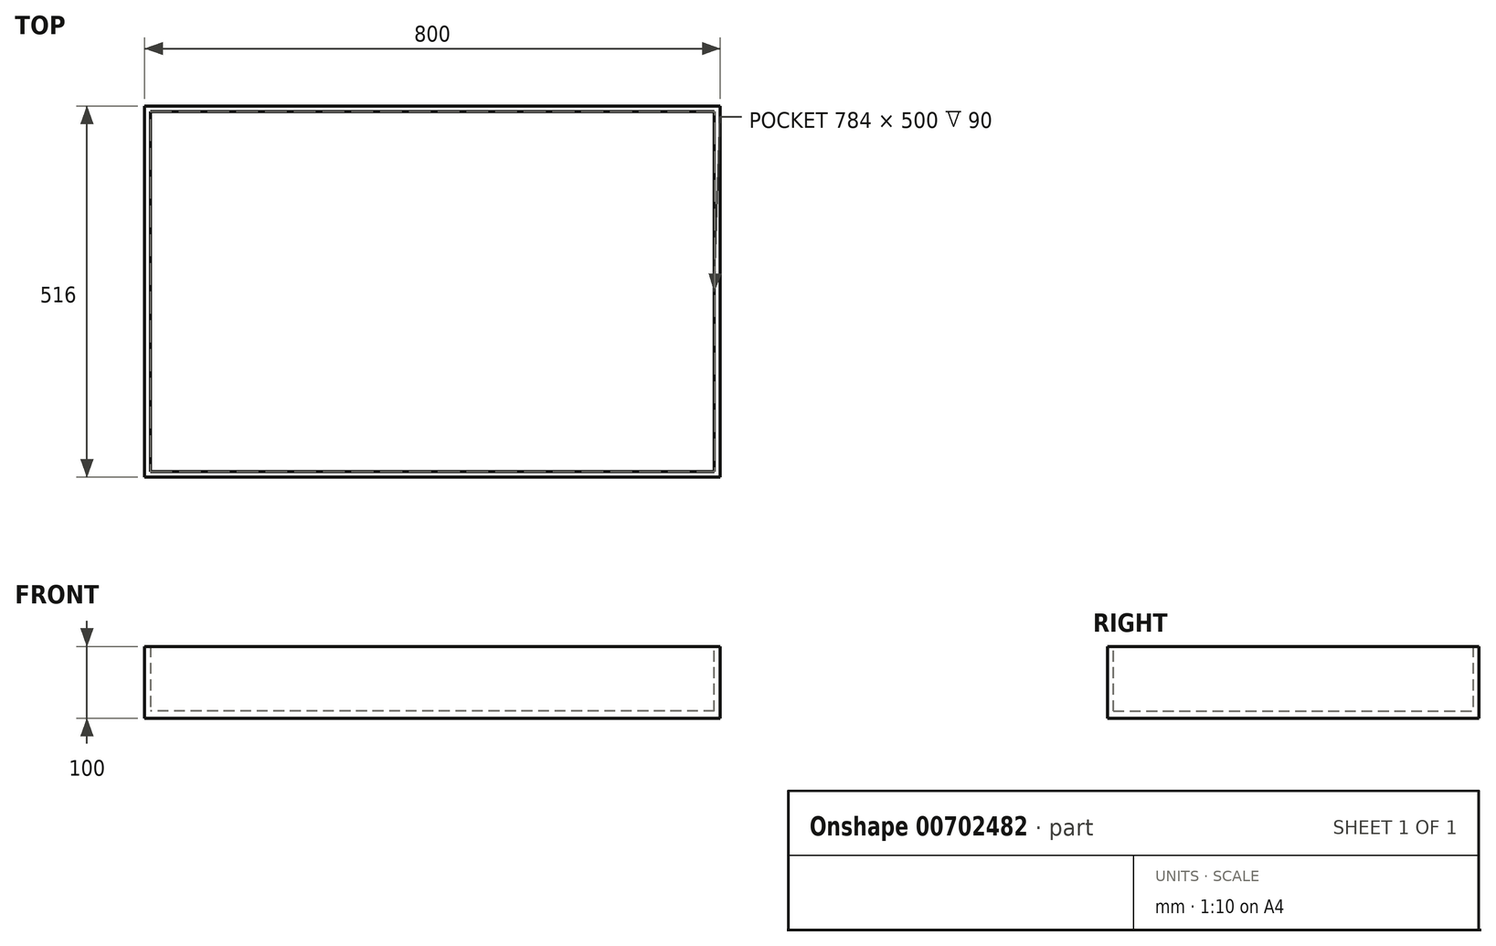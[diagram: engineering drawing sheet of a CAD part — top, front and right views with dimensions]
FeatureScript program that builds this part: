
annotation { "Feature Type Name" : "Feature", "Feature Type Description" : "" }
export const myFeature = defineFeature(function(context is Context, id is Id, definition is map)
    precondition{}
    {
        {
            var Q0;
            Q0=qCreatedBy(makeId("Front.planeOp"),FACE);
            var sketch = newSketch(context, id + "F0", { "sketchPlane" : qUnion([Q0])});
            skLineSegment(sketch, "E0.bottom", {"start": v(400, -50) * mm, "end": v(-400, -50) * mm});
            skLineSegment(sketch, "E0.top", {"start": v(400, 50) * mm, "end": v(-400, 50) * mm});
            skLineSegment(sketch, "E0.left", {"start": v(400, -50) * mm, "end": v(400, 50) * mm});
            skLineSegment(sketch, "E0.right", {"start": v(-400, -50) * mm, "end": v(-400, 50) * mm});
            skPoint(sketch, "E0.middle", {"position": v(0, 0) * mm});
            skSolve(sketch);
        }
        {
            var Q0;
            Q0=makeQuery(id+"F0.imprint","IMPRINT",FACE,{"disambiguationData":[TD([[makeQuery(id+"F0.imprint","IMPRINT",EDGE,{"derivedFrom":sQuery(id+"F0.wireOp",EDGE,"E0.bottom")}),-1.0]])]});
            extrude(context, id + "F1", {"entities" : qUnion([Q0]), "depth" : 8 * mm, "offsetDistance" : 25 * mm});
        }
        {
            var Q0;
            Q0=makeQuery(id+"F1.opExtrude","SWEPT_FACE",FACE,{"disambiguationData":[OSD([sQuery(id+"F0.wireOp",EDGE,"E0.left")])]});
            var sketch = newSketch(context, id + "F2", { "sketchPlane" : qUnion([Q0])});
            skLineSegment(sketch, "E1.bottom", {"start": v(0, 50) * mm, "end": v(500, 50) * mm});
            skLineSegment(sketch, "E1.top", {"start": v(0, -50) * mm, "end": v(500, -50) * mm});
            skLineSegment(sketch, "E1.left", {"start": v(0, 50) * mm, "end": v(0, -50) * mm});
            skLineSegment(sketch, "E1.right", {"start": v(500, 50) * mm, "end": v(500, -50) * mm});
            skSolve(sketch);
        }
        {
            var Q0;
            Q0=makeQuery(id+"F2.imprint","IMPRINT",FACE,{"disambiguationData":[TD([[makeQuery(id+"F2.imprint","IMPRINT",EDGE,{"derivedFrom":sQuery(id+"F2.wireOp",EDGE,"E1.bottom")}),-1.0]])]});
            extrude(context, id + "F3", {"entities" : qUnion([Q0]), "operationType" : NewBodyOperationType.ADD, "oppositeDirection" : true, "depth" : 8 * mm, "offsetDistance" : 25 * mm});
        }
        {
            var Q0;
            Q0=makeQuery(id+"F3.opExtrude","SWEPT_FACE",FACE,{"disambiguationData":[OSD([sQuery(id+"F2.wireOp",EDGE,"E1.right")])]});
            var sketch = newSketch(context, id + "F4", { "sketchPlane" : qUnion([Q0])});
            skLineSegment(sketch, "E2.bottom", {"start": v(-400, 50) * mm, "end": v(400, 50) * mm});
            skLineSegment(sketch, "E2.top", {"start": v(-400, -50) * mm, "end": v(400, -50) * mm});
            skLineSegment(sketch, "E2.left", {"start": v(-400, 50) * mm, "end": v(-400, -50) * mm});
            skLineSegment(sketch, "E2.right", {"start": v(400, 50) * mm, "end": v(400, -50) * mm});
            skSolve(sketch);
        }
        {
            var Q0;
            {var subQ2=sQuery(id+"F4.wireOp",EDGE,"E2.right");Q0=makeQuery(id+"F4.imprint","IMPRINT",FACE,{"disambiguationData":[TD([[makeQuery(id+"F4.imprint","IMPRINT",EDGE,{"derivedFrom":subQ2}),-1.0]])]});}
            var Q1;
            {var subQ0=sQuery(id+"F4.wireOp",EDGE,"E2.left");Q1=makeQuery(id+"F4.imprint","IMPRINT",FACE,{"disambiguationData":[TD([[makeQuery(id+"F4.imprint","IMPRINT",EDGE,{"derivedFrom":subQ0}),1.0]])]});}
            extrude(context, id + "F5", {"entities" : qUnion([Q0, Q1]), "operationType" : NewBodyOperationType.ADD, "depth" : 8 * mm, "offsetDistance" : 25 * mm});
        }
        {
            var Q0;
            Q0=makeQuery(id+"F5.opExtrude","SWEPT_FACE",FACE,{"disambiguationData":[OSD([sQuery(id+"F4.wireOp",EDGE,"E2.right")])]});
            var sketch = newSketch(context, id + "F6", { "sketchPlane" : qUnion([Q0])});
            skLineSegment(sketch, "E3.bottom", {"start": v(-500, 50) * mm, "end": v(0, 50) * mm});
            skLineSegment(sketch, "E3.top", {"start": v(-500, -50) * mm, "end": v(0, -50) * mm});
            skLineSegment(sketch, "E3.left", {"start": v(-500, 50) * mm, "end": v(-500, -50) * mm});
            skLineSegment(sketch, "E3.right", {"start": v(0, 50) * mm, "end": v(0, -50) * mm});
            skSolve(sketch);
        }
        {
            var Q0;
            Q0=makeQuery(id+"F6.imprint","IMPRINT",FACE,{"disambiguationData":[TD([[makeQuery(id+"F6.imprint","IMPRINT",EDGE,{"derivedFrom":sQuery(id+"F6.wireOp",EDGE,"E3.bottom")}),-1.0]])]});
            extrude(context, id + "F7", {"entities" : qUnion([Q0]), "operationType" : NewBodyOperationType.ADD, "oppositeDirection" : true, "depth" : 8 * mm, "offsetDistance" : 25 * mm});
        }
        {
            var Q0;
            Q0=makeQuery(id+"F7.boolean.opBoolean","MERGE",FACE,{"derivedFrom":[makeQuery(id+"F5.boolean.opBoolean","MERGE",FACE,{"derivedFrom":[makeQuery(id+"F3.boolean.opBoolean","MERGE",FACE,{"derivedFrom":[makeQuery(id+"F1.opExtrude","SWEPT_FACE",FACE,{"disambiguationData":[OSD([sQuery(id+"F0.wireOp",EDGE,"E0.bottom")])]}),makeQuery(id+"F3.opExtrude","SWEPT_FACE",FACE,{"disambiguationData":[OSD([sQuery(id+"F2.wireOp",EDGE,"E1.top")])]})]}),makeQuery(id+"F5.opExtrude","SWEPT_FACE",FACE,{"disambiguationData":[OSD([sQuery(id+"F4.wireOp",EDGE,"E2.top")])]})]}),makeQuery(id+"F7.opExtrude","SWEPT_FACE",FACE,{"disambiguationData":[OSD([sQuery(id+"F6.wireOp",EDGE,"E3.top")])]})]});
            var sketch = newSketch(context, id + "F8", { "sketchPlane" : qUnion([Q0])});
            skLineSegment(sketch, "E4.bottom", {"start": v(-392, 0) * mm, "end": v(392, 0) * mm});
            skLineSegment(sketch, "E4.top", {"start": v(-392, -500) * mm, "end": v(392, -500) * mm});
            skLineSegment(sketch, "E4.left", {"start": v(-392, 0) * mm, "end": v(-392, -500) * mm});
            skLineSegment(sketch, "E4.right", {"start": v(392, 0) * mm, "end": v(392, -500) * mm});
            skSolve(sketch);
        }
        {
            var Q0;
            Q0=makeQuery(id+"F8.imprint","IMPRINT",FACE,{"disambiguationData":[TD([[makeQuery(id+"F8.imprint","IMPRINT",EDGE,{"derivedFrom":sQuery(id+"F8.wireOp",EDGE,"E4.bottom")}),1.0]])]});
            extrude(context, id + "F9", {"entities" : qUnion([Q0]), "operationType" : NewBodyOperationType.ADD, "oppositeDirection" : true, "depth" : 10 * mm, "offsetDistance" : 25 * mm});
        }
    });
